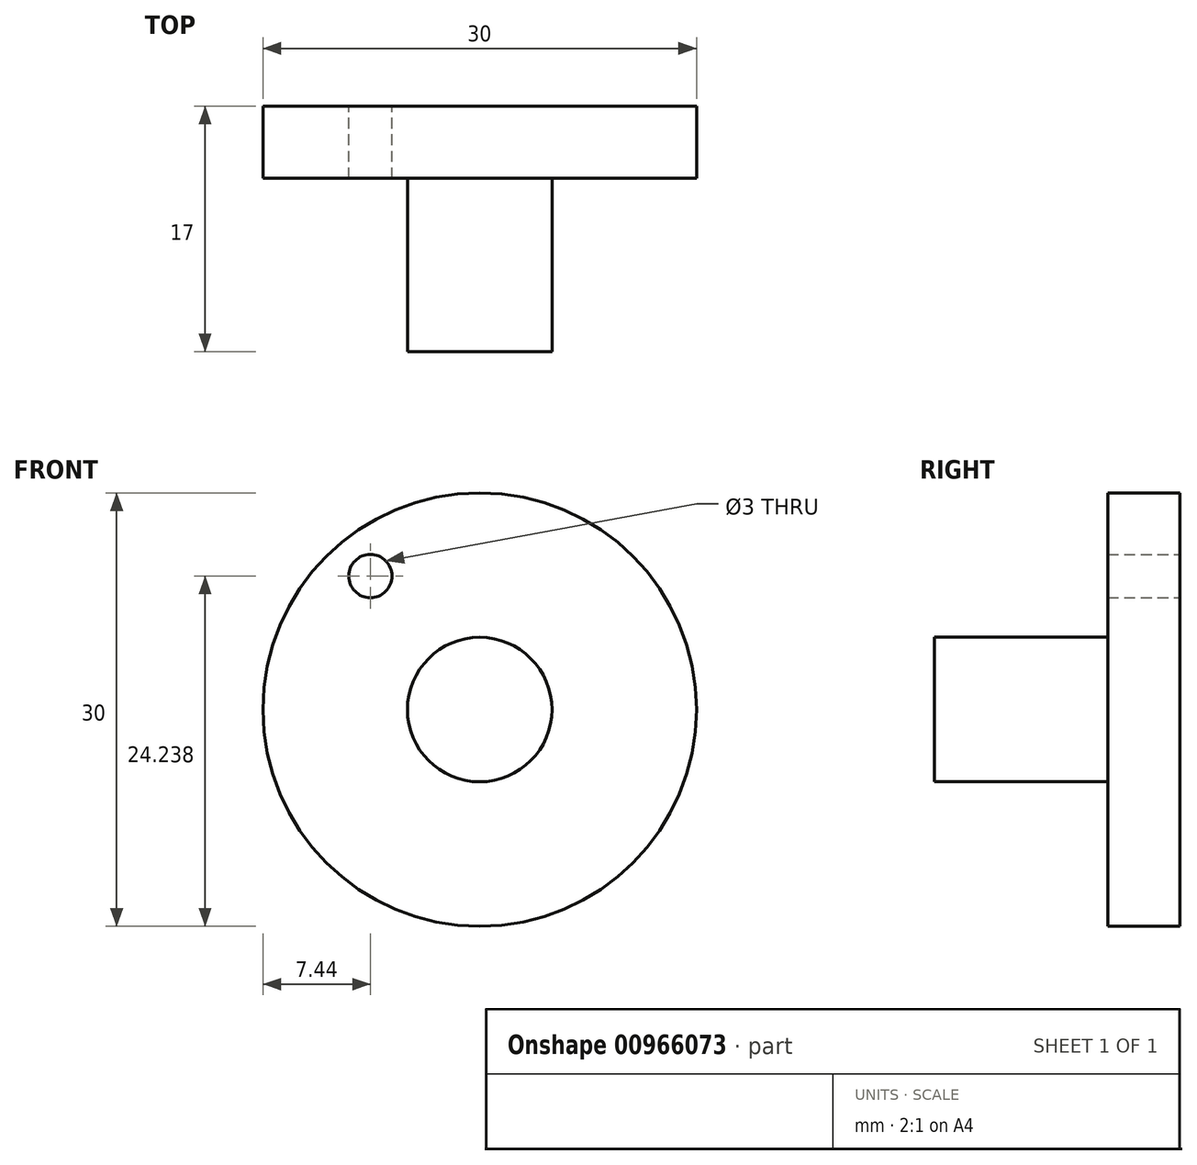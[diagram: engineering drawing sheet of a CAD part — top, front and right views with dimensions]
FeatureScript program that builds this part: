
annotation { "Feature Type Name" : "Feature", "Feature Type Description" : "" }
export const myFeature = defineFeature(function(context is Context, id is Id, definition is map)
    precondition{}
    {
        {
            var Q0;
            Q0=qCreatedBy(makeId("Front.planeOp"),FACE);
            var sketch = newSketch(context, id + "F0", { "sketchPlane" : qUnion([Q0])});
            skCircle(sketch, "E0", {"center": v(0, 0) * mm, "radius": 15 * mm});
            skSolve(sketch);
        }
        {
            var Q0;
            Q0=makeQuery(id+"F0.imprint","IMPRINT",FACE,{"disambiguationData":[TD([[makeQuery(id+"F0.imprint","IMPRINT",EDGE,{"derivedFrom":sQuery(id+"F0.wireOp",EDGE,"E0")}),1.0]])]});
            var sketch = newSketch(context, id + "F1", { "sketchPlane" : qUnion([Q0])});
            skCircle(sketch, "E1", {"center": v(-7.56, 9.24) * mm, "radius": 1.5 * mm});
            skSolve(sketch);
        }
        {
            var Q0;
            Q0 = qSketchRegion(id + "F0", true);
            extrude(context, id + "F2", {"entities" : qUnion([Q0]), "depth" : 5 * mm, "offsetDistance" : 25 * mm});
        }
        {
            var Q0;
            Q0 = qSketchRegion(id + "F1", true);
            extrude(context, id + "F3", {"entities" : qUnion([Q0]), "operationType" : NewBodyOperationType.REMOVE, "depth" : 6 * mm, "offsetDistance" : 25 * mm});
        }
        {
            var Q0;
            Q0=makeQuery(id+"F1.imprint","IMPRINT",FACE,{"disambiguationData":[TD([[makeQuery(id+"F1.imprint","IMPRINT",EDGE,{"derivedFrom":sQuery(id+"F1.wireOp",EDGE,"E1")}),-1.0]])]});
            var sketch = newSketch(context, id + "F4", { "sketchPlane" : qUnion([Q0])});
            skCircle(sketch, "E2", {"center": v(0, 0) * mm, "radius": 5 * mm});
            skSolve(sketch);
        }
        {
            var Q0;
            Q0 = qSketchRegion(id + "F4", true);
            extrude(context, id + "F5", {"entities" : qUnion([Q0]), "operationType" : NewBodyOperationType.ADD, "depth" : 17 * mm, "offsetDistance" : 25 * mm});
        }
    });
